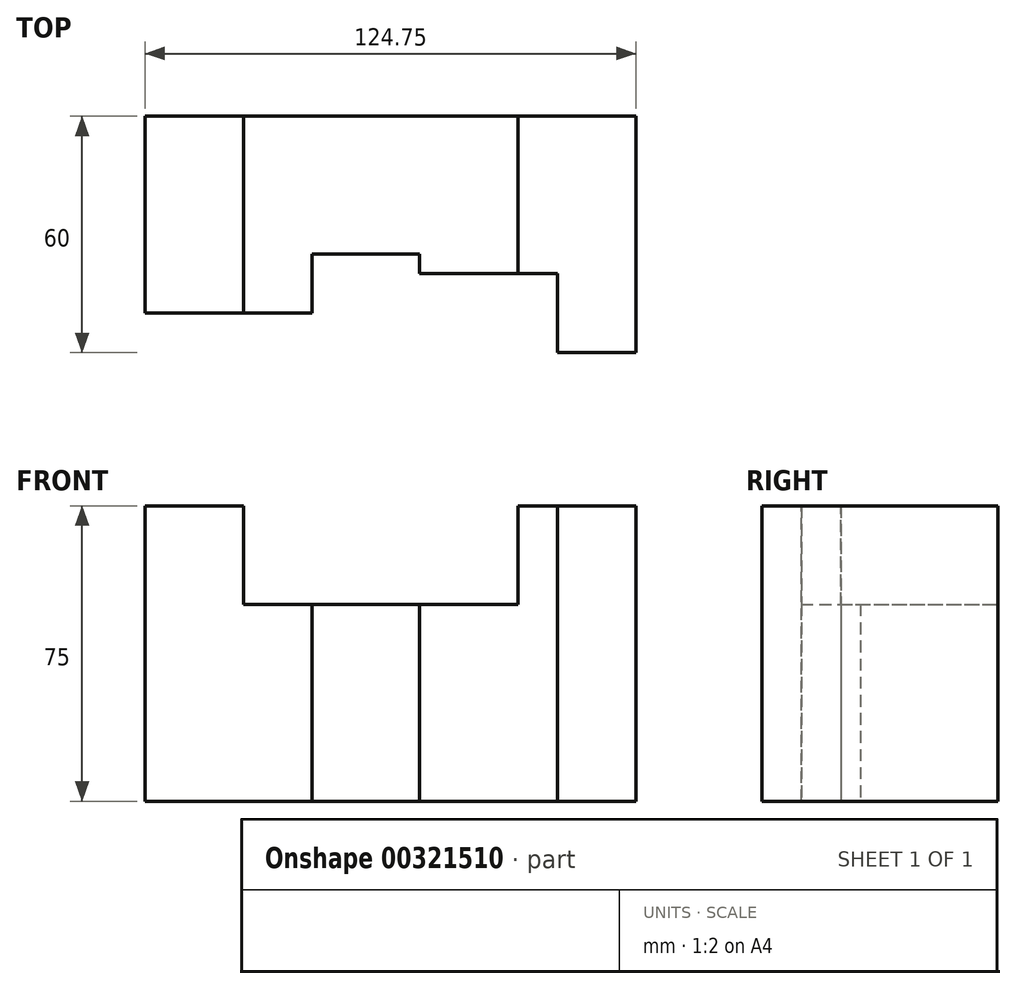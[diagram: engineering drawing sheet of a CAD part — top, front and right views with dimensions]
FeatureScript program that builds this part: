
annotation { "Feature Type Name" : "Feature", "Feature Type Description" : "" }
export const myFeature = defineFeature(function(context is Context, id is Id, definition is map)
    precondition{}
    {
        {
            var Q0;
            Q0=qCreatedBy(makeId("Front.planeOp"),FACE);
            var sketch = newSketch(context, id + "F0", { "sketchPlane" : qUnion([Q0])});
            skLineSegment(sketch, "E0", {"start": v(0, 0) * mm, "end": v(0, 75) * mm});
            skLineSegment(sketch, "E1", {"start": v(0, 75) * mm, "end": v(25, 75) * mm});
            skLineSegment(sketch, "E2", {"start": v(25, 75) * mm, "end": v(25, 50) * mm});
            skLineSegment(sketch, "E3", {"start": v(25, 50) * mm, "end": v(94.75, 50) * mm});
            skLineSegment(sketch, "E4", {"start": v(94.75, 50) * mm, "end": v(94.75, 75) * mm});
            skLineSegment(sketch, "E5", {"start": v(94.75, 75) * mm, "end": v(124.75, 75) * mm});
            skLineSegment(sketch, "E6", {"start": v(124.75, 75) * mm, "end": v(124.75, 0) * mm});
            skLineSegment(sketch, "E7", {"start": v(124.75, 0) * mm, "end": v(0, 0) * mm});
            skLineSegment(sketch, "E8", {"start": v(42.5, 50) * mm, "end": v(42.5, 0) * mm});
            skLineSegment(sketch, "E9", {"start": v(69.75, 50) * mm, "end": v(69.75, 0) * mm});
            skLineSegment(sketch, "E10", {"start": v(104.75, 75) * mm, "end": v(104.75, 0) * mm});
            skSolve(sketch);
        }
        {
            var Q0;
            {var subQ4=sQuery(id+"F0.wireOp",EDGE,"E0");Q0=makeQuery(id+"F0.imprint","IMPRINT",FACE,{"disambiguationData":[TD([[makeQuery(id+"F0.imprint","IMPRINT",EDGE,{"derivedFrom":subQ4}),-1.0]])]});}
            extrude(context, id + "F1", {"entities" : qUnion([Q0]), "depth" : 50 * mm});
        }
        {
            var Q0;
            {var subQ0=sQuery(id+"F0.wireOp",EDGE,"E8");Q0=makeQuery(id+"F0.imprint","IMPRINT",FACE,{"disambiguationData":[TD([[makeQuery(id+"F0.imprint","IMPRINT",EDGE,{"derivedFrom":subQ0}),1.0]])]});}
            extrude(context, id + "F2", {"entities" : qUnion([Q0]), "operationType" : NewBodyOperationType.ADD, "depth" : 35 * mm});
        }
        {
            var Q0;
            {var subQ1=sQuery(id+"F0.wireOp",EDGE,"E4");Q0=makeQuery(id+"F0.imprint","IMPRINT",FACE,{"disambiguationData":[TD([[makeQuery(id+"F0.imprint","IMPRINT",EDGE,{"derivedFrom":subQ1}),-1.0]])]});}
            extrude(context, id + "F3", {"entities" : qUnion([Q0]), "operationType" : NewBodyOperationType.ADD, "depth" : 40 * mm});
        }
        {
            var Q0;
            {var subQ0=sQuery(id+"F0.wireOp",EDGE,"E6");Q0=makeQuery(id+"F0.imprint","IMPRINT",FACE,{"disambiguationData":[TD([[makeQuery(id+"F0.imprint","IMPRINT",EDGE,{"derivedFrom":subQ0}),-1.0]])]});}
            extrude(context, id + "F4", {"entities" : qUnion([Q0]), "operationType" : NewBodyOperationType.ADD, "depth" : 60 * mm});
        }
    });
